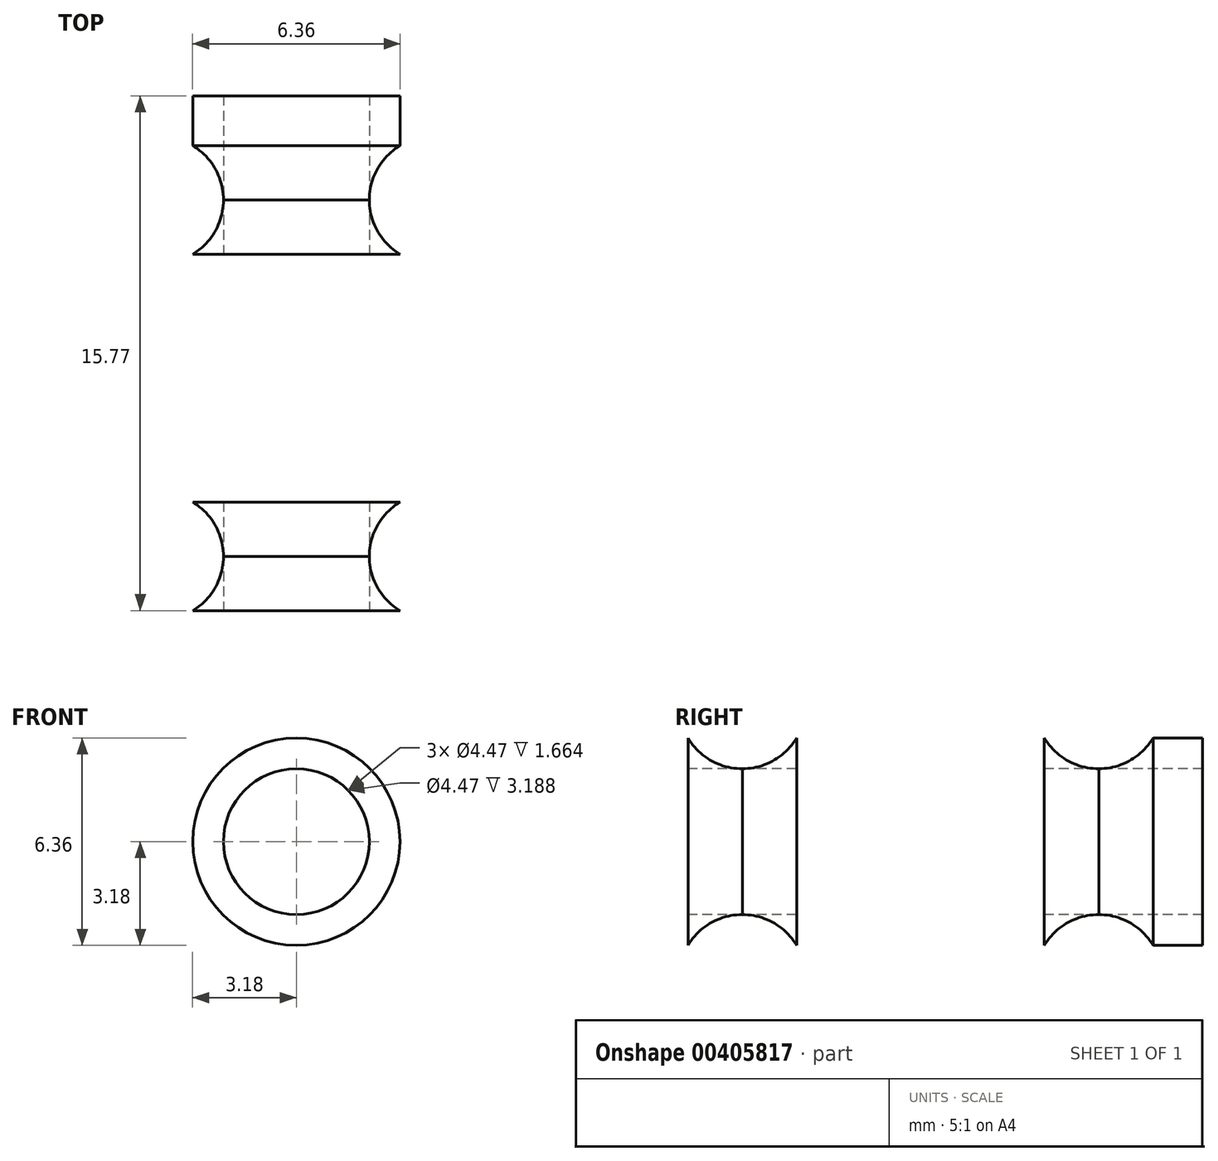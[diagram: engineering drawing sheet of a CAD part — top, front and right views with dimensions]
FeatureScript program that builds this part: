
annotation { "Feature Type Name" : "Feature", "Feature Type Description" : "" }
export const myFeature = defineFeature(function(context is Context, id is Id, definition is map)
    precondition{}
    {
        {
            var Q0;
            Q0=qCreatedBy(makeId("Top.planeOp"),FACE);
            var sketch = newSketch(context, id + "F0", { "sketchPlane" : qUnion([Q0])});
            skLineSegment(sketch, "E0", {"start": v(0, 8.65) * mm, "end": v(0, -8.65) * mm});
            skLineSegment(sketch, "E1.bottom", {"start": v(-3.17, 8.65) * mm, "end": v(3.18, 8.65) * mm});
            skLineSegment(sketch, "E1.top", {"start": v(-3.17, -8.65) * mm, "end": v(3.18, -8.65) * mm});
            skLineSegment(sketch, "E1.left", {"start": v(-3.18, 8.65) * mm, "end": v(-3.18, -8.65) * mm});
            skLineSegment(sketch, "E1.right", {"start": v(3.18, 8.65) * mm, "end": v(3.18, -8.65) * mm});
            skPoint(sketch, "E1.middle", {"position": v(0, 0) * mm});
            skLineSegment(sketch, "E2", {"start": v(-3.18, -7.12) * mm, "end": v(3.18, -7.12) * mm});
            skLineSegment(sketch, "E3", {"start": v(-3.18, -3.8) * mm, "end": v(3.18, -3.8) * mm});
            skLineSegment(sketch, "E4.bottom", {"start": v(-2.24, 8.65) * mm, "end": v(2.24, 8.65) * mm});
            skLineSegment(sketch, "E4.top", {"start": v(-2.24, -8.65) * mm, "end": v(2.24, -8.65) * mm});
            skLineSegment(sketch, "E4.left", {"start": v(-2.24, 8.65) * mm, "end": v(-2.24, -8.65) * mm});
            skLineSegment(sketch, "E4.right", {"start": v(2.24, 8.65) * mm, "end": v(2.24, -8.65) * mm});
            skCircle(sketch, "E5", {"center": v(4.18, -5.46) * mm, "radius": 1.94 * mm});
            skPoint(sketch, "E5.third.point", {"position": v(2.24, -5.46) * mm});
            skLineSegment(sketch, "E6.MirrorCS", {"start": v(3.17, -8.65) * mm, "end": v(-3.18, -8.65) * mm});
            skLineSegment(sketch, "E7.MirrorCS", {"start": v(3.17, 8.65) * mm, "end": v(-3.18, 8.65) * mm});
            skPoint(sketch, "E8.MirrorP", {"position": v(-2.24, -5.46) * mm});
            skLineSegment(sketch, "E9.MirrorCS", {"start": v(2.24, -8.65) * mm, "end": v(-2.24, -8.65) * mm});
            skLineSegment(sketch, "E10.MirrorCS", {"start": v(2.24, 8.65) * mm, "end": v(-2.24, 8.65) * mm});
            skLineSegment(sketch, "E11.MirrorCS", {"start": v(3.18, -7.12) * mm, "end": v(-3.18, -7.12) * mm});
            skLineSegment(sketch, "E12.MirrorCS", {"start": v(3.18, -3.8) * mm, "end": v(-3.18, -3.8) * mm});
            skCircle(sketch, "E13.MirrorC", {"center": v(-4.18, -5.46) * mm, "radius": 1.94 * mm});
            skLineSegment(sketch, "E14.MirrorCS", {"start": v(-3.18, 3.8) * mm, "end": v(3.18, 3.8) * mm});
            skLineSegment(sketch, "E15.MirrorCS", {"start": v(3.18, 7.12) * mm, "end": v(-3.18, 7.12) * mm});
            skLineSegment(sketch, "E16.MirrorCS", {"start": v(3.18, 3.8) * mm, "end": v(-3.18, 3.8) * mm});
            skLineSegment(sketch, "E17.MirrorCS", {"start": v(2.24, -8.65) * mm, "end": v(2.24, 8.65) * mm});
            skLineSegment(sketch, "E18.MirrorCS", {"start": v(-2.24, -8.65) * mm, "end": v(-2.24, 8.65) * mm});
            skLineSegment(sketch, "E19.MirrorCS", {"start": v(-3.18, 7.12) * mm, "end": v(3.17, 7.12) * mm});
            skLineSegment(sketch, "E20.MirrorCS", {"start": v(3.18, -8.65) * mm, "end": v(3.17, 8.65) * mm});
            skLineSegment(sketch, "E21.MirrorCS", {"start": v(0, -8.65) * mm, "end": v(0, 8.65) * mm});
            skLineSegment(sketch, "E22.MirrorCS", {"start": v(-3.18, -8.65) * mm, "end": v(-3.18, 8.65) * mm});
            skCircle(sketch, "E23.MirrorC", {"center": v(-4.18, 5.46) * mm, "radius": 1.94 * mm});
            skCircle(sketch, "E24.MirrorC", {"center": v(4.18, 5.46) * mm, "radius": 1.94 * mm});
            skLineSegment(sketch, "E25.MirrorCS", {"start": v(-3.17, -8.65) * mm, "end": v(-3.17, 8.65) * mm});
            skPoint(sketch, "E26.MirrorP", {"position": v(-2.24, 5.46) * mm});
            skLineSegment(sketch, "E27.MirrorCS", {"start": v(3.18, -8.65) * mm, "end": v(3.18, 8.65) * mm});
            skPoint(sketch, "E28.MirrorP", {"position": v(2.24, 5.46) * mm});
            skLineSegment(sketch, "E29", {"start": v(-4.7, -9.77) * mm, "end": v(4.7, -9.77) * mm});
            skSolve(sketch);
        }
        {
            var Q0;
            {var subQ0=sQuery(id+"F0.wireOp",EDGE,"E4.top");var subQ1=sQuery(id+"F0.wireOp",EDGE,"E21.MirrorCS");var subQ2=makeQuery(id+"F0.imprint","INTERSECT",VERTEX,{"derivedFrom":[subQ1,subQ0]});Q0=makeQuery(id+"F0.imprint","IMPRINT",FACE,{"disambiguationData":[TD([[makeQuery(id+"F0.imprint","IMPRINT",EDGE,{"disambiguationData":[TD([[subQ2,-1.0]])],"derivedFrom":subQ1}),1.0]])]});}
            var Q1;
            {var subQ3=sQuery(id+"F0.wireOp",EDGE,"E4.left");var subQ5=sQuery(id+"F0.wireOp",EDGE,"E11.MirrorCS");var subQ7=makeQuery(id+"F0.imprint","INTERSECT",VERTEX,{"derivedFrom":[subQ5,subQ3]});Q1=makeQuery(id+"F0.imprint","IMPRINT",FACE,{"disambiguationData":[TD([[makeQuery(id+"F0.imprint","IMPRINT",EDGE,{"disambiguationData":[TD([[subQ7,-1.0]])],"derivedFrom":subQ5}),1.0]])]});}
            var Q2;
            {var subQ1=sQuery(id+"F0.wireOp",EDGE,"E11.MirrorCS");var subQ3=sQuery(id+"F0.wireOp",EDGE,"E4.left");var subQ4=makeQuery(id+"F0.imprint","INTERSECT",VERTEX,{"derivedFrom":[subQ1,subQ3]});Q2=makeQuery(id+"F0.imprint","IMPRINT",FACE,{"disambiguationData":[TD([[makeQuery(id+"F0.imprint","IMPRINT",EDGE,{"disambiguationData":[TD([[subQ4,1.0]])],"derivedFrom":subQ3}),-1.0]])]});}
            var Q3;
            {var subQ1=sQuery(id+"F0.wireOp",EDGE,"E12.MirrorCS");var subQ3=sQuery(id+"F0.wireOp",EDGE,"E4.left");var subQ4=makeQuery(id+"F0.imprint","INTERSECT",VERTEX,{"derivedFrom":[subQ1,subQ3]});Q3=makeQuery(id+"F0.imprint","IMPRINT",FACE,{"disambiguationData":[TD([[makeQuery(id+"F0.imprint","IMPRINT",EDGE,{"disambiguationData":[TD([[subQ4,-1.0]])],"derivedFrom":subQ3}),-1.0]])]});}
            var Q4;
            {var subQ0=sQuery(id+"F0.wireOp",EDGE,"E11.MirrorCS");var subQ1=sQuery(id+"F0.wireOp",EDGE,"E21.MirrorCS");var subQ2=makeQuery(id+"F0.imprint","INTERSECT",VERTEX,{"derivedFrom":[subQ1,subQ0]});Q4=makeQuery(id+"F0.imprint","IMPRINT",FACE,{"disambiguationData":[TD([[makeQuery(id+"F0.imprint","IMPRINT",EDGE,{"disambiguationData":[TD([[subQ2,-1.0]])],"derivedFrom":subQ1}),1.0]])]});}
            var Q5;
            {var subQ0=sQuery(id+"F0.wireOp",EDGE,"E12.MirrorCS");var subQ1=sQuery(id+"F0.wireOp",EDGE,"E21.MirrorCS");var subQ2=makeQuery(id+"F0.imprint","INTERSECT",VERTEX,{"derivedFrom":[subQ1,subQ0]});Q5=makeQuery(id+"F0.imprint","IMPRINT",FACE,{"disambiguationData":[TD([[makeQuery(id+"F0.imprint","IMPRINT",EDGE,{"disambiguationData":[TD([[subQ2,-1.0]])],"derivedFrom":subQ1}),1.0]])]});}
            var Q6;
            {var subQ1=sQuery(id+"F0.wireOp",EDGE,"E12.MirrorCS");var subQ3=sQuery(id+"F0.wireOp",EDGE,"E4.left");var subQ4=makeQuery(id+"F0.imprint","INTERSECT",VERTEX,{"derivedFrom":[subQ1,subQ3]});Q6=makeQuery(id+"F0.imprint","IMPRINT",FACE,{"disambiguationData":[TD([[makeQuery(id+"F0.imprint","IMPRINT",EDGE,{"disambiguationData":[TD([[subQ4,1.0]])],"derivedFrom":subQ3}),-1.0]])]});}
            var Q7;
            {var subQ1=sQuery(id+"F0.wireOp",EDGE,"E16.MirrorCS");var subQ3=sQuery(id+"F0.wireOp",EDGE,"E4.left");var subQ4=makeQuery(id+"F0.imprint","INTERSECT",VERTEX,{"derivedFrom":[subQ1,subQ3]});Q7=makeQuery(id+"F0.imprint","IMPRINT",FACE,{"disambiguationData":[TD([[makeQuery(id+"F0.imprint","IMPRINT",EDGE,{"disambiguationData":[TD([[subQ4,-1.0]])],"derivedFrom":subQ3}),-1.0]])]});}
            var Q8;
            {var subQ0=sQuery(id+"F0.wireOp",EDGE,"RgFoMQd6-mJ7p-L36l-cqsI-ruaDX4uavil2.bottom");var subQ1=sQuery(id+"F0.wireOp",EDGE,"E21.MirrorCS");var subQ2=makeQuery(id+"F0.imprint","INTERSECT",VERTEX,{"derivedFrom":[subQ1,subQ0]});Q8=makeQuery(id+"F0.imprint","IMPRINT",FACE,{"disambiguationData":[TD([[makeQuery(id+"F0.imprint","IMPRINT",EDGE,{"disambiguationData":[TD([[subQ2,-1.0]])],"derivedFrom":subQ1}),1.0]])]});}
            var Q9;
            {var subQ1=sQuery(id+"F0.wireOp",EDGE,"E16.MirrorCS");var subQ3=sQuery(id+"F0.wireOp",EDGE,"E4.left");var subQ4=makeQuery(id+"F0.imprint","INTERSECT",VERTEX,{"derivedFrom":[subQ1,subQ3]});Q9=makeQuery(id+"F0.imprint","IMPRINT",FACE,{"disambiguationData":[TD([[makeQuery(id+"F0.imprint","IMPRINT",EDGE,{"disambiguationData":[TD([[subQ4,1.0]])],"derivedFrom":subQ3}),-1.0]])]});}
            var Q10;
            {var subQ1=sQuery(id+"F0.wireOp",EDGE,"E15.MirrorCS");var subQ3=sQuery(id+"F0.wireOp",EDGE,"E4.left");var subQ4=makeQuery(id+"F0.imprint","INTERSECT",VERTEX,{"derivedFrom":[subQ1,subQ3]});Q10=makeQuery(id+"F0.imprint","IMPRINT",FACE,{"disambiguationData":[TD([[makeQuery(id+"F0.imprint","IMPRINT",EDGE,{"disambiguationData":[TD([[subQ4,-1.0]])],"derivedFrom":subQ3}),-1.0]])]});}
            var Q11;
            {var subQ4=sQuery(id+"F0.wireOp",EDGE,"E16.MirrorCS");var subQ5=sQuery(id+"F0.wireOp",EDGE,"E21.MirrorCS");var subQ6=makeQuery(id+"F0.imprint","INTERSECT",VERTEX,{"derivedFrom":[subQ5,subQ4]});Q11=makeQuery(id+"F0.imprint","IMPRINT",FACE,{"disambiguationData":[TD([[makeQuery(id+"F0.imprint","IMPRINT",EDGE,{"disambiguationData":[TD([[subQ6,-1.0]])],"derivedFrom":subQ5}),1.0]])]});}
            var Q12;
            {var subQ0=sQuery(id+"F0.wireOp",EDGE,"E4.bottom");var subQ1=sQuery(id+"F0.wireOp",EDGE,"E21.MirrorCS");var subQ2=makeQuery(id+"F0.imprint","INTERSECT",VERTEX,{"derivedFrom":[subQ1,subQ0]});Q12=makeQuery(id+"F0.imprint","IMPRINT",FACE,{"disambiguationData":[TD([[makeQuery(id+"F0.imprint","IMPRINT",EDGE,{"disambiguationData":[TD([[subQ2,1.0]])],"derivedFrom":subQ1}),1.0]])]});}
            var Q13;
            {var subQ0=sQuery(id+"F0.wireOp",EDGE,"E1.left");var subQ1=sQuery(id+"F0.wireOp",EDGE,"E1.bottom");var subQ2=makeQuery(id+"F0.imprint","INTERSECT",VERTEX,{"derivedFrom":[subQ1,subQ0]});Q13=makeQuery(id+"F0.imprint","IMPRINT",FACE,{"disambiguationData":[TD([[makeQuery(id+"F0.imprint","IMPRINT",EDGE,{"disambiguationData":[TD([[subQ2,-1.0]])],"derivedFrom":subQ1}),-1.0]])]});}
            var Q14;
            Q14=sQuery(id+"F0.wireOp",EDGE,"E21.MirrorCS");
            revolve(context, id + "F1", {"entities" : qUnion([Q0, Q1, Q2, Q3, Q4, Q5, Q6, Q7, Q8, Q9, Q10, Q11, Q12, Q13]), "axis" : qUnion([Q14]), "revolveType" : RevolveType.FULL});
        }
    });
